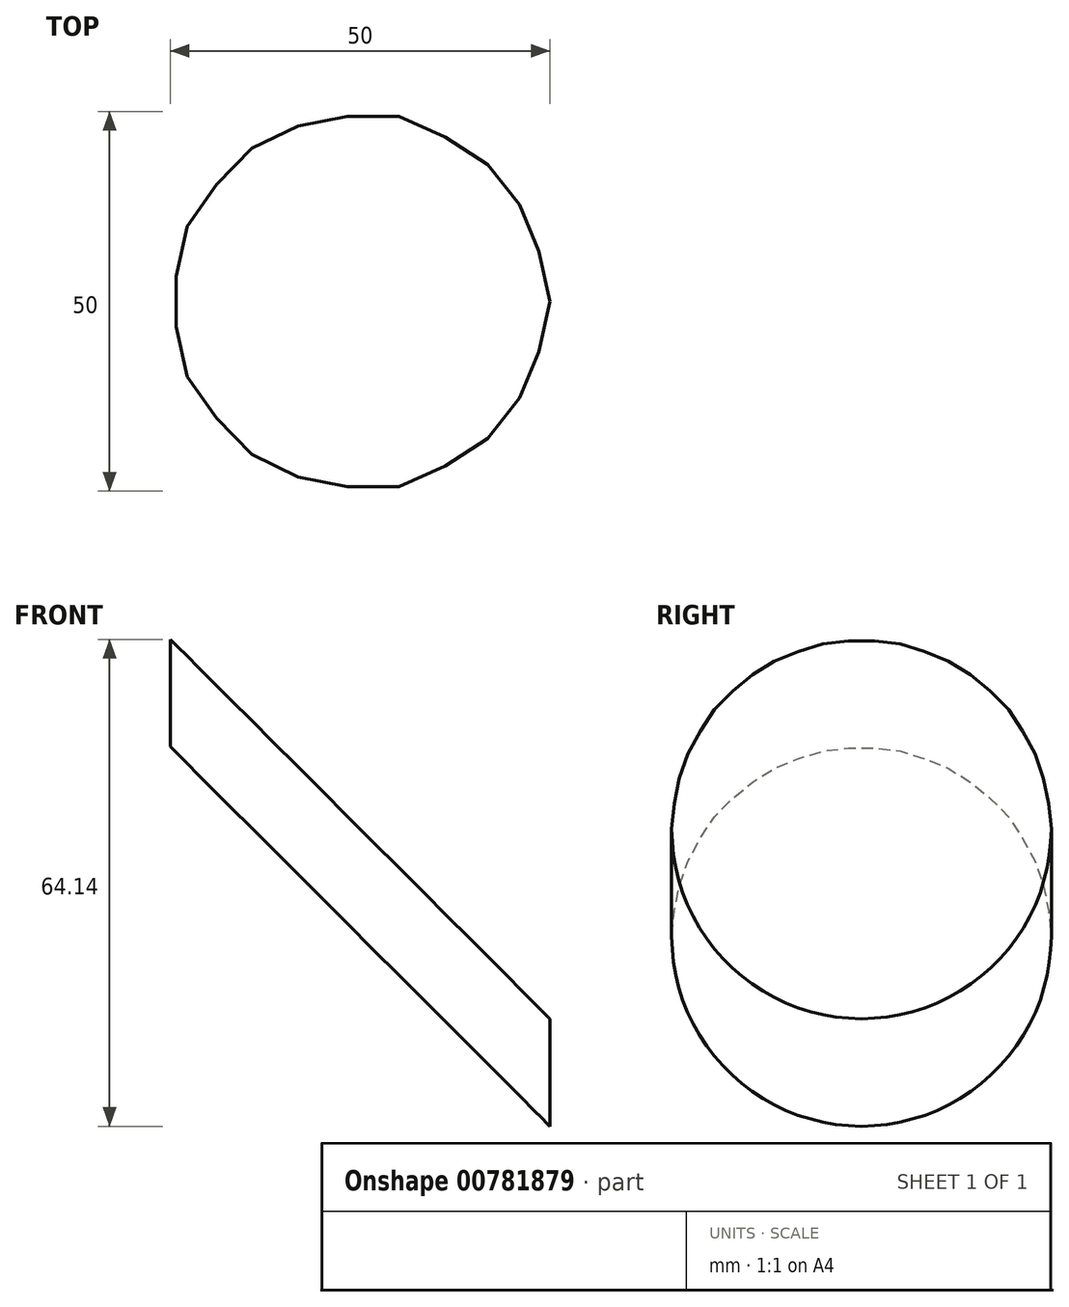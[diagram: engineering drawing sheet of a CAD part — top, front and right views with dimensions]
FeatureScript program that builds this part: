
annotation { "Feature Type Name" : "Feature", "Feature Type Description" : "" }
export const myFeature = defineFeature(function(context is Context, id is Id, definition is map)
    precondition{}
    {
        {
            var Q0;
            Q0=qCreatedBy(makeId("Top.planeOp"),FACE);
            var sketch = newSketch(context, id + "F0", { "sketchPlane" : qUnion([Q0])});
            skCircle(sketch, "E0", {"center": v(0, 0) * mm, "radius": 25 * mm});
            skSolve(sketch);
        }
        {
            var Q0;
            Q0=qSketchRegion(id+"F0",true);
            extrude(context, id + "F1", {"entities" : qUnion([Q0]), "depth" : 64.14 * mm});
        }
        {
            var Q0;
            Q0=qCreatedBy(makeId("Front.planeOp"),FACE);
            var sketch = newSketch(context, id + "F2", { "sketchPlane" : qUnion([Q0])});
            skLineSegment(sketch, "E1.0", {"start": v(-25, 64.14) * mm, "end": v(25, 64.14) * mm});
            skLineSegment(sketch, "E2.0", {"start": v(-25, 0) * mm, "end": v(25, 0) * mm});
            skLineSegment(sketch, "E3", {"start": v(-25, 64.14) * mm, "end": v(25, 14.14) * mm});
            skLineSegment(sketch, "E4", {"start": v(25, 14.14) * mm, "end": v(25, 64.14) * mm});
            skLineSegment(sketch, "E5", {"start": v(-25, 0) * mm, "end": v(-25, 50) * mm});
            skLineSegment(sketch, "E6", {"start": v(-25, 50) * mm, "end": v(25, 0) * mm});
            skSolve(sketch);
        }
        {
            var Q0;
            Q0=qSketchRegion(id+"F2",true);
            extrude(context, id + "F3", {"entities" : qUnion([Q0]), "operationType" : NewBodyOperationType.REMOVE, "endBound" : BoundingType.THROUGH_ALL, "oppositeDirection" : true, "depth" : 25 * mm, "hasSecondDirection" : true, "secondDirectionBound" : SecondDirectionBoundingType.THROUGH_ALL, "secondDirectionOppositeDirection" : false, "secondDirectionDepth" : 25 * mm});
        }
    });
